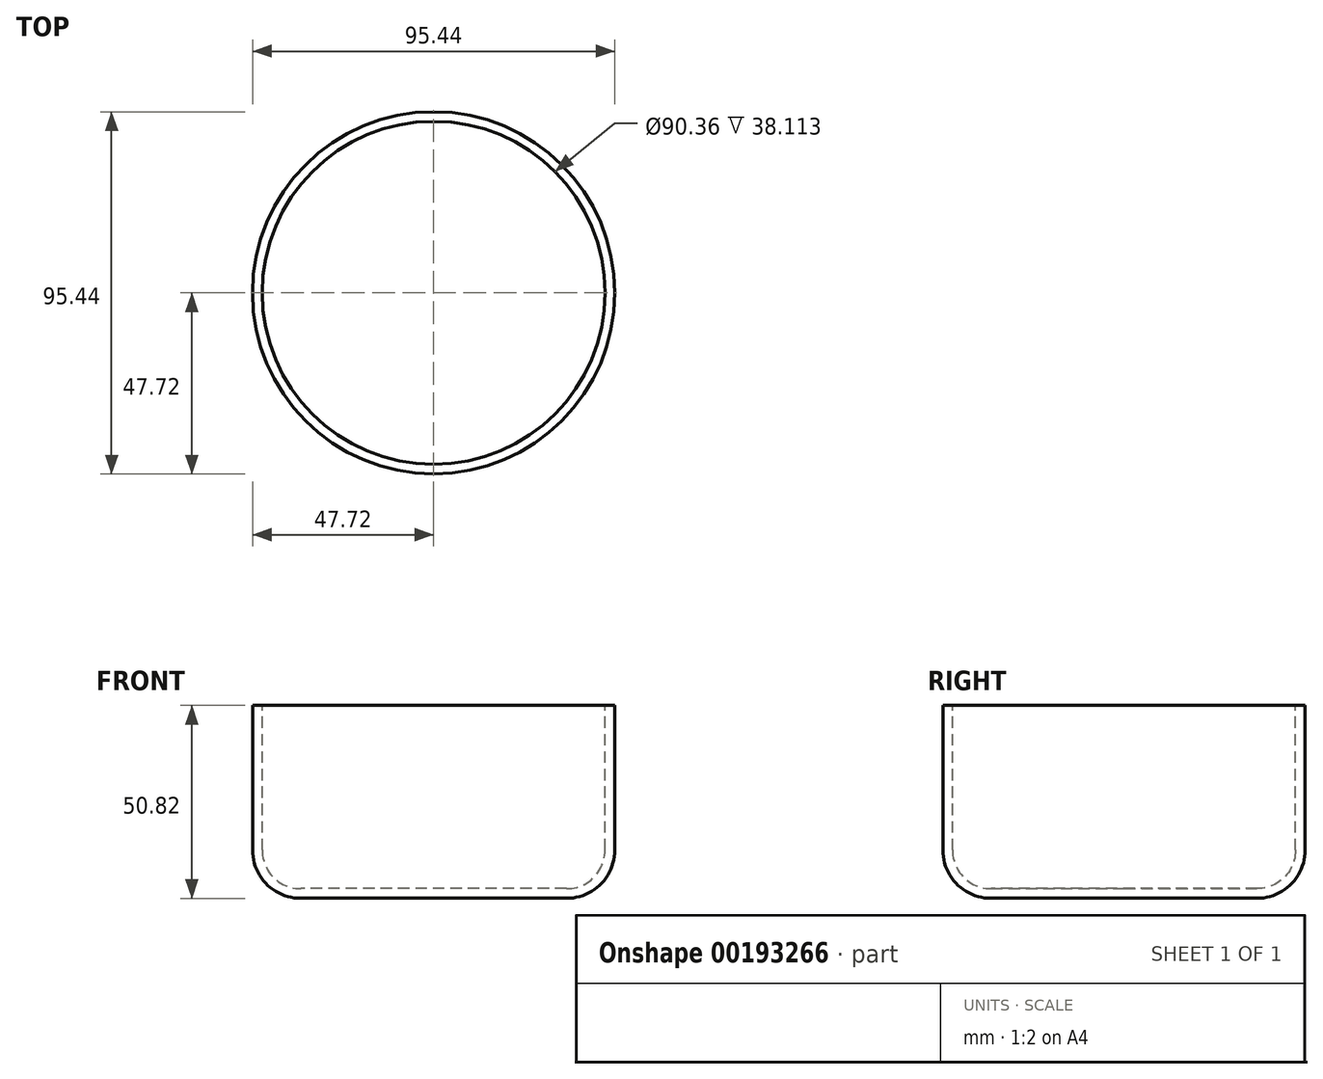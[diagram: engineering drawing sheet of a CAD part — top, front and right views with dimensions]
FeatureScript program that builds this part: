
annotation { "Feature Type Name" : "Feature", "Feature Type Description" : "" }
export const myFeature = defineFeature(function(context is Context, id is Id, definition is map)
    precondition{}
    {
        {
            var Q0;
            Q0=qCreatedBy(makeId("Front.planeOp"),FACE);
            var sketch = newSketch(context, id + "F0", { "sketchPlane" : qUnion([Q0])});
            skLineSegment(sketch, "E0", {"start": v(-47.72, 28.06) * mm, "end": v(-47.72, -10.06) * mm});
            skLineSegment(sketch, "E1", {"start": v(-35.02, -22.76) * mm, "end": v(0, -22.76) * mm});
            skPoint(sketch, "E2.visualSharp", {"position": v(-47.72, -22.76) * mm});
            skArc(sketch, "E2.filletArc", {"start": v(-47.72, -10.06) * mm, "mid": v(-44, -19.04) * mm, "end": v(-35.02, -22.76) * mm});
            skLineSegment(sketch, "E3", {"start": v(-47.72, 28.06) * mm, "end": v(0, 28.06) * mm});
            skLineSegment(sketch, "E4", {"start": v(0, 28.06) * mm, "end": v(0, -22.76) * mm});
            skSolve(sketch);
        }
        {
            var Q0;
            Q0 = qSketchRegion(id + "F0", true);
            var Q1;
            Q1=sQuery(id+"F0.wireOp",EDGE,"E4");
            revolve(context, id + "F1", {"entities" : qUnion([Q0]), "axis" : qUnion([Q1]), "revolveType" : RevolveType.FULL});
        }
        {
            var Q0;
            Q0=makeQuery(id+"F1.opRevolve","SWEPT_FACE",FACE,{"disambiguationData":[OSD([sQuery(id+"F0.wireOp",EDGE,"E3")])]});
            shell(context, id + "F2", {"entities" : qUnion([Q0]), "thickness" : 2.54 * mm});
        }
    });
